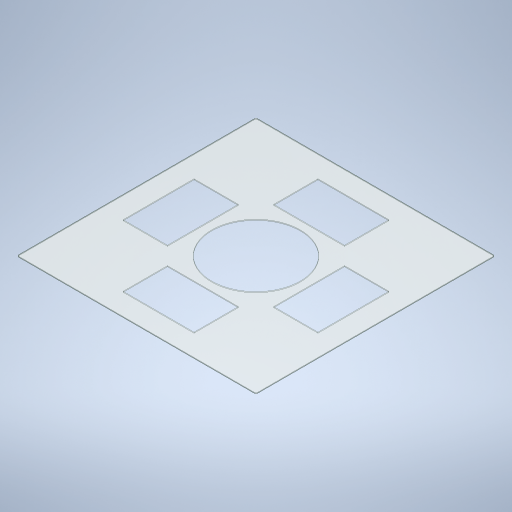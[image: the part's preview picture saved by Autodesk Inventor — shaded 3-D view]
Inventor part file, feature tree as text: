
AUTODESK INVENTOR PART (.ipt)
format: ipt  version: 2023 (Build 270158000, 158)  size: 333,824 bytes
history: native  units: in
note: dims shown in document units (in); Inventor stores cm internally (conversion verified against a paired STEP export)
features: extrude x1, chamfer x1, sketch x1
ambient origin geometry x8: Origin, YZ Plane, XZ Plane, XY Plane, X Axis, Y Axis, Z Axis, Center Point
bodies: Solid1 (feature_tree)
feature tree (3):
  extrude  "Extrusion1"  Depth=54.0in
  chamfer  "Chamfer1"  Distance=1.0in
  sketch  "Sketch1"  dims[d0=54.0in d1=54.0in d2=1.0in d3=1.0in d4=8.0in d5=16.0in d6=8.0in d7=16.0in d8=16.0in d9=8.0in d10=16.0in d11=8.0in d12=4.0in d13=4.0in d14=4.0in d15=4.0in d16=17.0in d17=17.0in d18=17.0in d19=17.0in d20=20.0in d21=1.0in d22=1.0in d23=1.0in d24=1.0in d25=45.0deg d26=2.5in d27=45.0deg d28=45.0deg d29=45.0deg d30=1.0in d31=1.0in d32=1.0in d33=1.0in d34=0.25in d35=0.25in d36=0.25in d37=0.25in d38=0.25in d39=0.25in d40=0.25in d41=0.25in d42=0.2in d43=0.0in d44=0.06in d45=0.125in d46=45.0deg]
